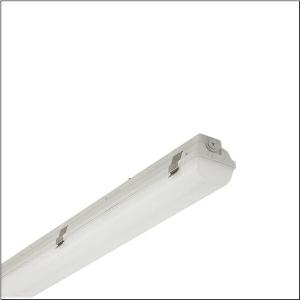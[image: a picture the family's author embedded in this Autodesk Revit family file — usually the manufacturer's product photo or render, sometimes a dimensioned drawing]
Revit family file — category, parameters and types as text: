
# Revit family: monsun_r__21_eco_51fj20mp47a_a802
name_source: partatom
category: Lighting Fixtures
units: mm (PartAtom-declared; Revit-internal decimal feet)

## family parameters
Cut with Voids When Loaded = No
Host = Face
Light Source = No
Part Type = Normal
Room Calculation Point = No
Round Connector Dimension = Use Diameter
Shared = No

## types (1)
- --- (1 x LED, 6600 lm, 50 W, 4000K)
    Apparent Load = 50 VA
    CIE Flux Codes = 40 69 88 88 100
    Color Rendering = 80
    Color Temperature = 4000K
    Default Elevation = 1800 mm
    Description = Monsun® 21 Eco, damp-proof luminaire, primary optical cover: diffuser, of PC, UV-stabilised, frosted, light emission: direct distribution, primary light characteristic: symmetric, installation type: suspended mounting, surface-mounted, LED, rated luminous flux: 6.600lm, luminous efficacy: 132lm/W, light colour: 840, colour temperature: 4000K, control gear: ECG Multilumen, with terminal, 3-pole, max. 2.5mm², mains connection: 220..240V, AC, 50/60Hz, rated input power: 50W, housing, of glass-fibre reinforced polyester, light grey (RAL 7035), length: 1.577mm, width: 90mm, height: 95mm, clip for enclosure, of spring steel V2A, protection rating (complete): IP66, insulation class (complete): insulation class I (protective earthing), certification: CE, UKCA, protection symbol: D, impact resistance: IK08, permissible operating ambient temperature: -20..+35°C, corresponds to IFS (International Featured Standards) requirements for safety and quality in the food industry, contact your sales advisor before using the luminaires in applications with unclear chemical exposure, large temperature fluctuations or condensation-forming humidity, packaging unit: 1 piece
    Height = 103 mm
    Lamp = 1 x LED
    Lamp Light Flux = 6600 lm
    Lamp Power = 50 W
    Lamp count = 1
    Length = 1577 mm
    Luminous efficacy = 132 lm/W
    Manufacturer = Siteco
    ModVariant = No
    Model = 51FJ20MP47A
    Mounting Place = Ceiling
    Mounting Type = Surface mounted
    Number of Poles = 1
    OnlyDefault = Yes
    Power Factor = 1
    Product Name = Monsun® 21 Eco
    Product group = damp-proof luminaire
    ProductGroupID = 300
    Protection Class = Protection class I
    Protection Degree = IP 66
    RLX_Detail_Level = 1
    RLX_Emergency_Light_Flux = 0 lm
    RLX_Emergency_Type = 0
    RLX_Emergency_Type_DB = No
    RlxData = <blob elided: 34141 chars, md5=f92a970c>
    Socket = socket
    Standby Power = 0 W
    System Light Flux = 6600 lm
    System Power = 50 W
    Type Comments = factory setting: luminous flux: 100 % | (ON | ON) | 350 mA
    Type Image = l_1007218.jpg
    URL = http://relux.com
    VarID = @adj_077797
    Voltage = 0 V
    Weight = 0.00 kg
    Width = 90 mm

## geometry (parser evidence)
native form markers: Blend x4, Sweep x13
no freeform markers — native parametric forms only
